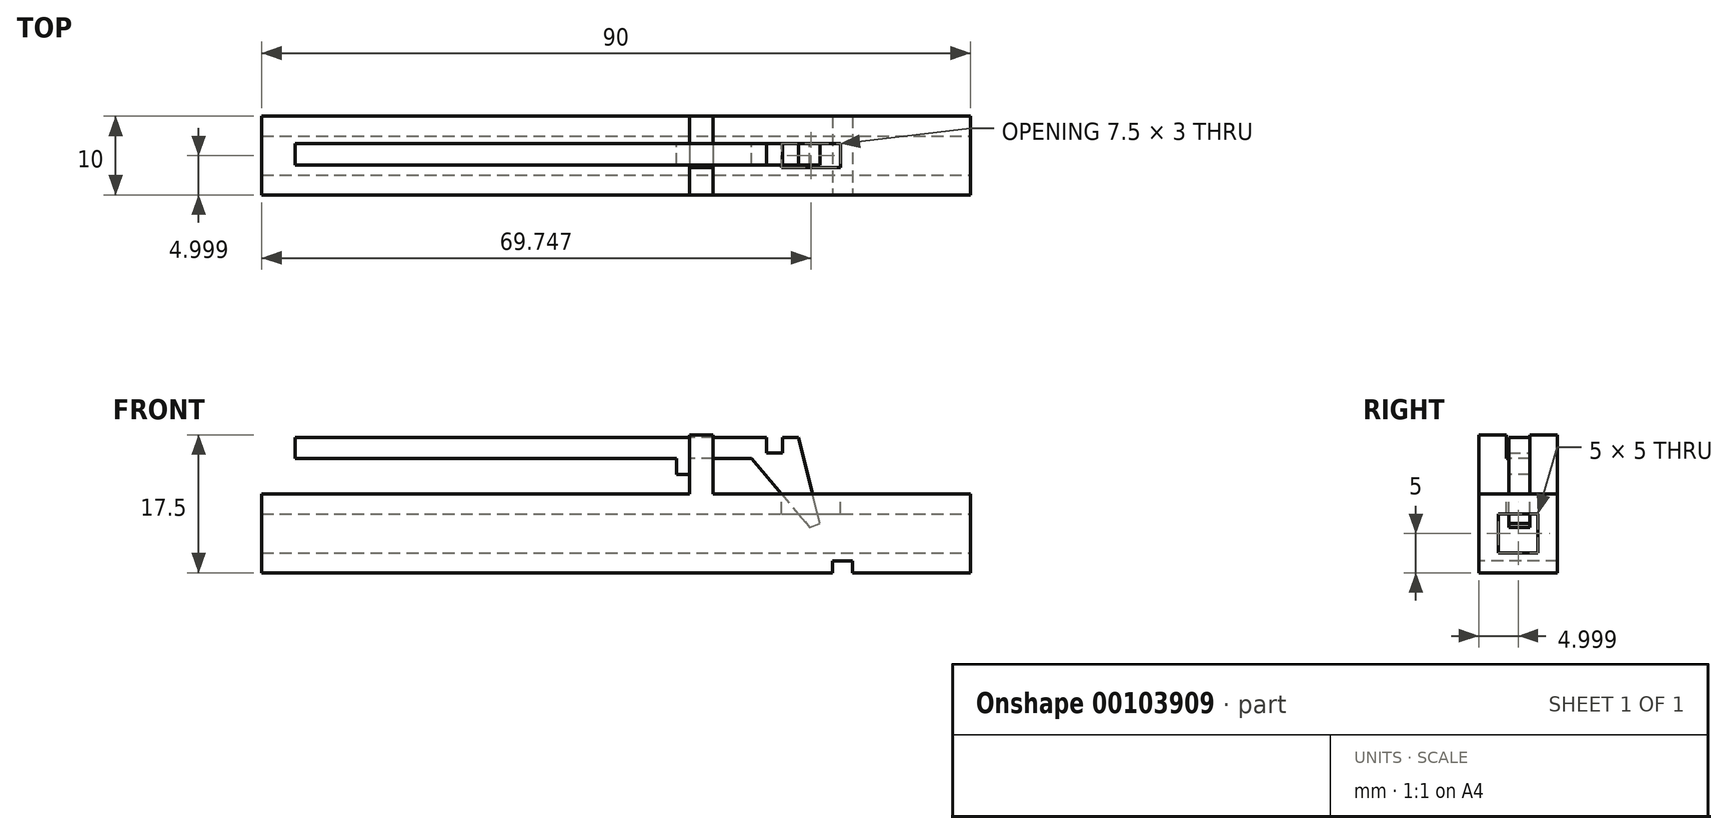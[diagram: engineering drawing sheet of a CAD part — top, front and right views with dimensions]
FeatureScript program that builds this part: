
annotation { "Feature Type Name" : "Feature", "Feature Type Description" : "" }
export const myFeature = defineFeature(function(context is Context, id is Id, definition is map)
    precondition{}
    {
        {
            var Q0;
            Q0=qCreatedBy(makeId("Top.planeOp"),FACE);
            var sketch = newSketch(context, id + "F0", { "sketchPlane" : qUnion([Q0])});
            skLineSegment(sketch, "E0.bottom", {"start": v(-30.23, 2.66) * mm, "end": v(59.77, 2.66) * mm});
            skLineSegment(sketch, "E0.top", {"start": v(-30.23, -7.34) * mm, "end": v(59.77, -7.34) * mm});
            skLineSegment(sketch, "E0.left", {"start": v(-30.23, 2.66) * mm, "end": v(-30.23, -7.34) * mm});
            skLineSegment(sketch, "E0.right", {"start": v(59.77, 2.66) * mm, "end": v(59.77, -7.34) * mm});
            skSolve(sketch);
        }
        {
            var Q0;
            Q0=makeQuery(id+"F0.imprint","IMPRINT",FACE,{"disambiguationData":[TD([[makeQuery(id+"F0.imprint","IMPRINT",EDGE,{"derivedFrom":sQuery(id+"F0.wireOp",EDGE,"E0.bottom")}),-1.0]])]});
            extrude(context, id + "F1", {"entities" : qUnion([Q0]), "depth" : 10 * mm});
        }
        {
            var Q0;
            Q0=makeQuery(id+"F1.opExtrude","SWEPT_FACE",FACE,{"disambiguationData":[OSD([sQuery(id+"F0.wireOp",EDGE,"E0.right")])]});
            var Q1;
            Q1=makeQuery(id+"F1.opExtrude","SWEPT_FACE",FACE,{"disambiguationData":[OSD([sQuery(id+"F0.wireOp",EDGE,"E0.left")])]});
            shell(context, id + "F2", {"entities" : qUnion([Q0, Q1]), "thickness" : 2.5 * mm});
        }
        {
            var Q0;
            Q0=makeQuery(id+"F1.opExtrude","CAP_FACE",FACE,{"disambiguationData":[OSD([sQuery(id+"F0.wireOp",EDGE,"E0.bottom"),sQuery(id+"F0.wireOp",EDGE,"E0.top"),sQuery(id+"F0.wireOp",EDGE,"E0.left"),sQuery(id+"F0.wireOp",EDGE,"E0.right")])],"isStart":false});
            var sketch = newSketch(context, id + "F3", { "sketchPlane" : qUnion([Q0])});
            skLineSegment(sketch, "E1.bottom", {"start": v(43.27, -0.84) * mm, "end": v(35.77, -0.84) * mm});
            skLineSegment(sketch, "E1.top", {"start": v(43.27, -3.84) * mm, "end": v(35.77, -3.84) * mm});
            skLineSegment(sketch, "E1.left", {"start": v(43.27, -0.84) * mm, "end": v(43.27, -3.84) * mm});
            skLineSegment(sketch, "E1.right", {"start": v(35.77, -0.84) * mm, "end": v(35.77, -3.84) * mm});
            skSolve(sketch);
        }
        {
            var Q0;
            Q0=makeQuery(id+"F3.imprint","IMPRINT",FACE,{"disambiguationData":[TD([[makeQuery(id+"F3.imprint","IMPRINT",EDGE,{"derivedFrom":sQuery(id+"F3.wireOp",EDGE,"E1.bottom")}),1.0]])]});
            extrude(context, id + "F4", {"entities" : qUnion([Q0]), "operationType" : NewBodyOperationType.REMOVE, "endBound" : BoundingType.UP_TO_NEXT, "oppositeDirection" : true, "depth" : 25 * mm});
        }
        {
            var Q0;
            Q0=makeQuery(id+"F1.opExtrude","CAP_FACE",FACE,{"disambiguationData":[OSD([sQuery(id+"F0.wireOp",EDGE,"E0.bottom"),sQuery(id+"F0.wireOp",EDGE,"E0.top"),sQuery(id+"F0.wireOp",EDGE,"E0.left"),sQuery(id+"F0.wireOp",EDGE,"E0.right")])],"isStart":false});
            var sketch = newSketch(context, id + "F5", { "sketchPlane" : qUnion([Q0])});
            skLineSegment(sketch, "E2.bottom", {"start": v(27.12, 2.66) * mm, "end": v(24.12, 2.66) * mm});
            skLineSegment(sketch, "E2.top", {"start": v(27.12, -7.34) * mm, "end": v(24.12, -7.34) * mm});
            skLineSegment(sketch, "E2.left", {"start": v(27.12, 2.66) * mm, "end": v(27.12, -7.34) * mm});
            skLineSegment(sketch, "E2.right", {"start": v(24.12, 2.66) * mm, "end": v(24.12, -7.34) * mm});
            skSolve(sketch);
        }
        {
            var Q0;
            Q0=makeQuery(id+"F5.imprint","IMPRINT",FACE,{"disambiguationData":[TD([[makeQuery(id+"F5.imprint","IMPRINT",EDGE,{"derivedFrom":sQuery(id+"F5.wireOp",EDGE,"E2.bottom")}),-1.0]])]});
            extrude(context, id + "F6", {"entities" : qUnion([Q0]), "operationType" : NewBodyOperationType.ADD, "depth" : 7.5 * mm});
        }
        {
            var Q0;
            Q0=makeQuery(id+"F6.opExtrude","CAP_FACE",FACE,{"disambiguationData":[OSD([sQuery(id+"F5.wireOp",EDGE,"E2.bottom"),sQuery(id+"F5.wireOp",EDGE,"E2.top"),sQuery(id+"F5.wireOp",EDGE,"E2.left"),sQuery(id+"F5.wireOp",EDGE,"E2.right")])],"isStart":false});
            var sketch = newSketch(context, id + "F7", { "sketchPlane" : qUnion([Q0])});
            skLineSegment(sketch, "E3", {"start": v(27.12, 2.66) * mm, "end": v(27.12, -0.84) * mm});
            skLineSegment(sketch, "E4.bottom", {"start": v(27.12, -0.84) * mm, "end": v(24.12, -0.84) * mm});
            skLineSegment(sketch, "E4.top", {"start": v(27.12, -3.84) * mm, "end": v(24.12, -3.84) * mm});
            skLineSegment(sketch, "E4.left", {"start": v(27.12, -0.84) * mm, "end": v(27.12, -3.84) * mm});
            skLineSegment(sketch, "E4.right", {"start": v(24.12, -0.84) * mm, "end": v(24.12, -3.84) * mm});
            skSolve(sketch);
        }
        {
            var Q0;
            Q0=makeQuery(id+"F7.imprint","IMPRINT",FACE,{"disambiguationData":[TD([[makeQuery(id+"F7.imprint","IMPRINT",EDGE,{"derivedFrom":sQuery(id+"F7.wireOp",EDGE,"E4.bottom")}),1.0]])]});
            extrude(context, id + "F8", {"entities" : qUnion([Q0]), "operationType" : NewBodyOperationType.REMOVE, "oppositeDirection" : true, "depth" : 3 * mm});
        }
        {
            var Q0;
            Q0=makeQuery(id+"F8.boolean.opBoolean","COPY",FACE,{"derivedFrom":makeQuery(id+"F8.opExtrude","SWEPT_FACE",FACE,{"disambiguationData":[OSD([sQuery(id+"F7.wireOp",EDGE,"E4.bottom")])]})});
            var sketch = newSketch(context, id + "F9", { "sketchPlane" : qUnion([Q0])});
            skLineSegment(sketch, "E5", {"start": v(32, 14.5) * mm, "end": v(39.38, 5.77) * mm});
            skPoint(sketch, "E5.startSnap0", {"position": v(25.62, 14.5) * mm});
            skLineSegment(sketch, "E6", {"start": v(39.38, 5.77) * mm, "end": v(40.68, 6.26) * mm});
            skLineSegment(sketch, "E7", {"start": v(40.68, 6.26) * mm, "end": v(37.94, 17.2) * mm});
            skLineSegment(sketch, "E8", {"start": v(37.94, 17.2) * mm, "end": v(-26, 17.2) * mm});
            skLineSegment(sketch, "E9", {"start": v(32, 14.5) * mm, "end": v(-26, 14.5) * mm});
            skLineSegment(sketch, "E10", {"start": v(-26, 14.5) * mm, "end": v(-26, 17.2) * mm});
            skSolve(sketch);
        }
        {
            var Q0;
            {var subQ6=sQuery(id+"F9.wireOp",EDGE,"E5");Q0=makeQuery(id+"F9.imprint","IMPRINT",FACE,{"disambiguationData":[TD([[makeQuery(id+"F9.imprint","IMPRINT",EDGE,{"derivedFrom":subQ6}),1.0]])]});}
            var Q1;
            {var subQ0=sQuery(id+"F9.wireOp",EDGE,"E8");var subQ1=sQuery(id+"F7.wireOp",EDGE,"E4.bottom");var subQ2=makeQuery(id+"F8.boolean.opBoolean","COPY",EDGE,{"derivedFrom":makeQuery(id+"F8.opExtrude","SWEPT_EDGE",EDGE,{"disambiguationData":[OSD([sQuery(id+"F7.wireOp",EDGE,"E3"),subQ1,sQuery(id+"F7.wireOp",EDGE,"E4.left")])]})});var subQ3=makeQuery(id+"F9.imprint","INTERSECT",VERTEX,{"derivedFrom":[subQ2,subQ0]});Q1=makeQuery(id+"F9.imprint","IMPRINT",FACE,{"disambiguationData":[TD([[makeQuery(id+"F9.imprint","IMPRINT",EDGE,{"disambiguationData":[TD([[subQ3,-1.0]])],"derivedFrom":subQ0}),1.0]])]});}
            var Q2;
            {var subQ0=sQuery(id+"F9.wireOp",EDGE,"E10");Q2=makeQuery(id+"F9.imprint","IMPRINT",FACE,{"disambiguationData":[TD([[makeQuery(id+"F9.imprint","IMPRINT",EDGE,{"derivedFrom":subQ0}),-1.0]])]});}
            extrude(context, id + "F10", {"entities" : qUnion([Q0, Q1, Q2]), "operationType" : NewBodyOperationType.ADD, "depth" : 2.7 * mm});
        }
        {
            var Q0;
            {var subQ1=sQuery(id+"F9.wireOp",EDGE,"E9");Q0=makeQuery(id+"F10.boolean.opBoolean","SPLIT",FACE,{"disambiguationData":[TD([makeQuery(id+"F6.opExtrude","SWEPT_FACE",FACE,{"disambiguationData":[OSD([sQuery(id+"F5.wireOp",EDGE,"E2.right")])]})])],"derivedFrom":makeQuery(id+"F10.opExtrude","SWEPT_FACE",FACE,{"disambiguationData":[OSD([subQ1])]})});}
            var sketch = newSketch(context, id + "F11", { "sketchPlane" : qUnion([Q0])});
            skLineSegment(sketch, "E11.bottom", {"start": v(24.12, 3.54) * mm, "end": v(22.48, 3.54) * mm});
            skLineSegment(sketch, "E11.top", {"start": v(24.12, 0.84) * mm, "end": v(22.48, 0.84) * mm});
            skLineSegment(sketch, "E11.left", {"start": v(24.12, 3.54) * mm, "end": v(24.12, 0.84) * mm});
            skLineSegment(sketch, "E11.right", {"start": v(22.48, 3.54) * mm, "end": v(22.48, 0.84) * mm});
            skSolve(sketch);
        }
        {
            var Q0;
            Q0=makeQuery(id+"F11.imprint","IMPRINT",FACE,{"disambiguationData":[TD([[makeQuery(id+"F11.imprint","IMPRINT",EDGE,{"derivedFrom":sQuery(id+"F11.wireOp",EDGE,"E11.bottom")}),1.0]])]});
            extrude(context, id + "F12", {"entities" : qUnion([Q0]), "operationType" : NewBodyOperationType.ADD, "depth" : 2 * mm});
        }
        {
            var Q0;
            Q0=makeQuery(id+"F10.opExtrude","SWEPT_FACE",FACE,{"disambiguationData":[OSD([sQuery(id+"F9.wireOp",EDGE,"E8")])]});
            var sketch = newSketch(context, id + "F13", { "sketchPlane" : qUnion([Q0])});
            skLineSegment(sketch, "E12.left", {"start": v(35.92, -3.54) * mm, "end": v(35.92, -0.84) * mm});
            skLineSegment(sketch, "E13", {"start": v(35.92, -0.84) * mm, "end": v(33.88, -0.84) * mm});
            skLineSegment(sketch, "E14", {"start": v(33.88, -0.84) * mm, "end": v(33.88, -3.54) * mm});
            skLineSegment(sketch, "E15", {"start": v(33.88, -3.54) * mm, "end": v(35.92, -3.54) * mm});
            skSolve(sketch);
        }
        {
            var Q0;
            Q0=makeQuery(id+"F13.imprint","IMPRINT",FACE,{"disambiguationData":[TD([[makeQuery(id+"F13.imprint","IMPRINT",EDGE,{"derivedFrom":sQuery(id+"F13.wireOp",EDGE,"E12.left")}),1.0]])]});
            extrude(context, id + "F14", {"entities" : qUnion([Q0]), "operationType" : NewBodyOperationType.REMOVE, "oppositeDirection" : true, "depth" : 2 * mm});
        }
        {
            var Q0;
            Q0=makeQuery(id+"F1.opExtrude","CAP_FACE",FACE,{"disambiguationData":[OSD([sQuery(id+"F0.wireOp",EDGE,"E0.bottom"),sQuery(id+"F0.wireOp",EDGE,"E0.top"),sQuery(id+"F0.wireOp",EDGE,"E0.left"),sQuery(id+"F0.wireOp",EDGE,"E0.right")])],"isStart":true});
            var sketch = newSketch(context, id + "F15", { "sketchPlane" : qUnion([Q0])});
            skLineSegment(sketch, "E16.bottom", {"start": v(42.3, -2.66) * mm, "end": v(44.85, -2.66) * mm});
            skLineSegment(sketch, "E16.top", {"start": v(42.3, 7.34) * mm, "end": v(44.85, 7.34) * mm});
            skLineSegment(sketch, "E16.left", {"start": v(42.3, -2.66) * mm, "end": v(42.3, 7.34) * mm});
            skLineSegment(sketch, "E16.right", {"start": v(44.85, -2.66) * mm, "end": v(44.85, 7.34) * mm});
            skSolve(sketch);
        }
        {
            var Q0;
            Q0=makeQuery(id+"F15.imprint","IMPRINT",FACE,{"disambiguationData":[TD([[makeQuery(id+"F15.imprint","IMPRINT",EDGE,{"derivedFrom":sQuery(id+"F15.wireOp",EDGE,"E16.bottom")}),1.0]])]});
            extrude(context, id + "F16", {"entities" : qUnion([Q0]), "operationType" : NewBodyOperationType.REMOVE, "oppositeDirection" : true, "depth" : 1.5 * mm});
        }
    });
